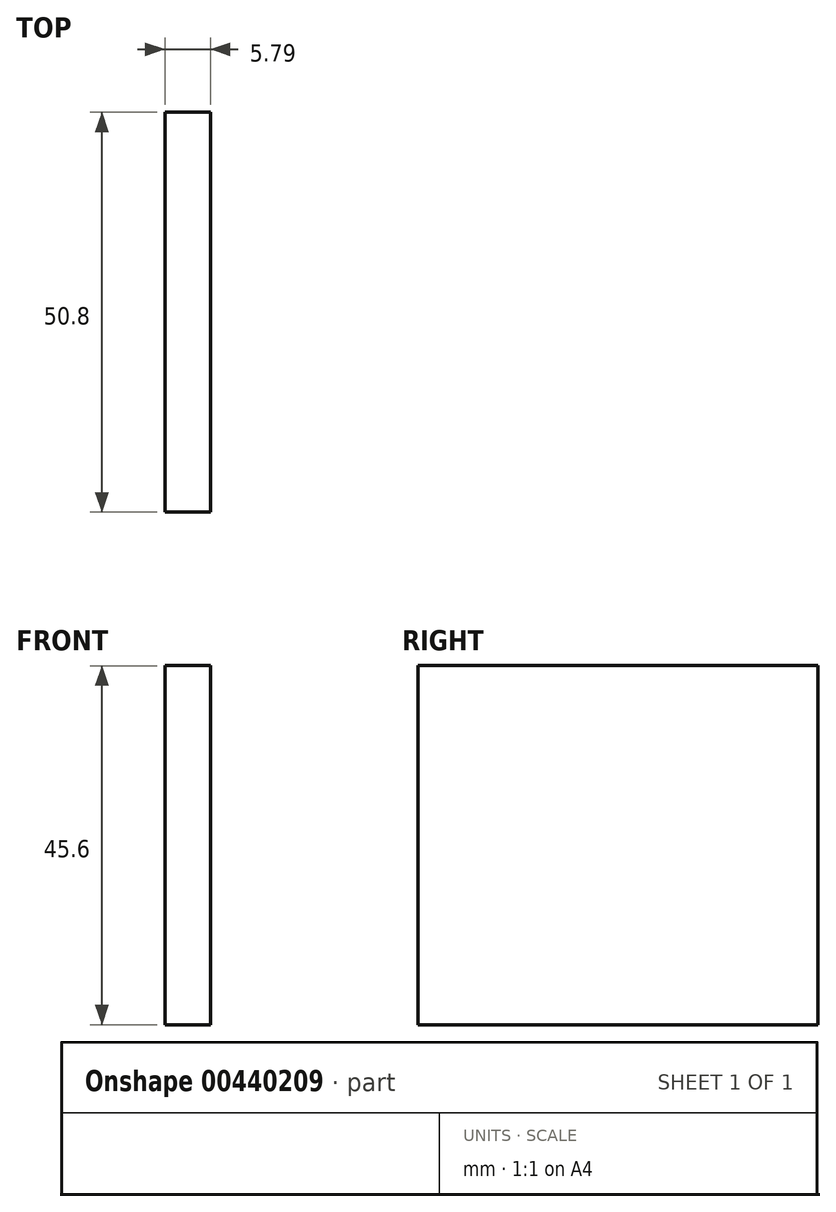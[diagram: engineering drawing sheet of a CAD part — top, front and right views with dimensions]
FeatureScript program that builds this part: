
annotation { "Feature Type Name" : "Feature", "Feature Type Description" : "" }
export const myFeature = defineFeature(function(context is Context, id is Id, definition is map)
    precondition{}
    {
        {
            var Q0;
            Q0=qCreatedBy(makeId("Front.planeOp"),FACE);
            var sketch = newSketch(context, id + "F0", { "sketchPlane" : qUnion([Q0])});
            skLineSegment(sketch, "E0", {"start": v(-25.79, 27.47) * mm, "end": v(-25.79, -18.13) * mm});
            skLineSegment(sketch, "E1", {"start": v(-25.79, -18.13) * mm, "end": v(-20, -18.13) * mm});
            skLineSegment(sketch, "E2", {"start": v(-20, -18.13) * mm, "end": v(-20, 27.47) * mm});
            skLineSegment(sketch, "E3", {"start": v(-20, 27.47) * mm, "end": v(-25.79, 27.47) * mm});
            skSolve(sketch);
        }
        {
            var Q0;
            Q0 = qSketchRegion(id + "F0", true);
            extrude(context, id + "F1", {"entities" : qUnion([Q0]), "depth" : 50.8 * mm});
        }
    });
